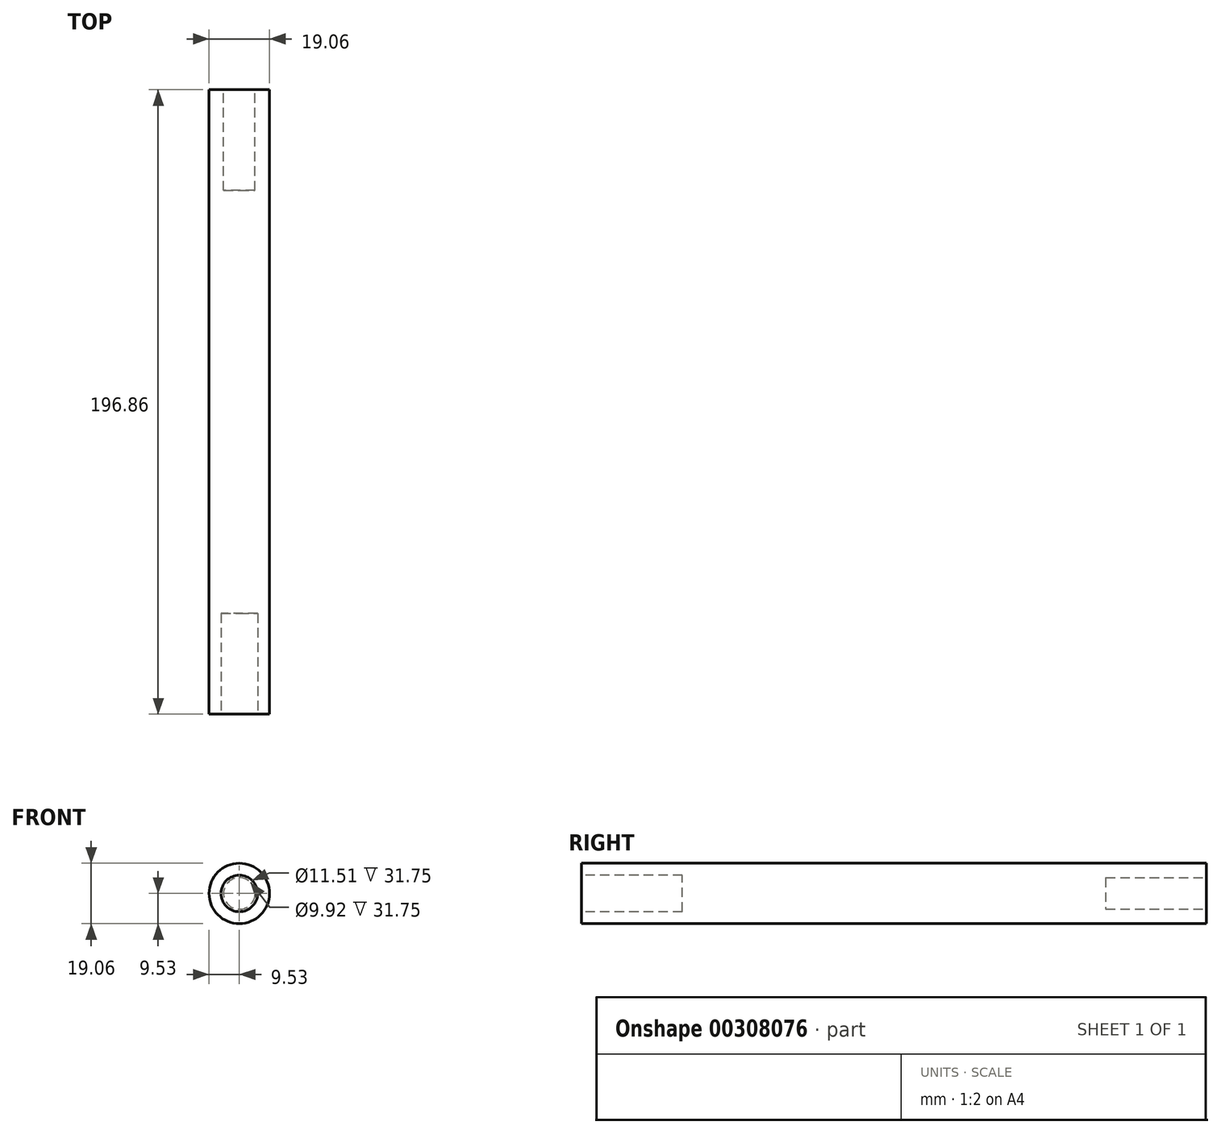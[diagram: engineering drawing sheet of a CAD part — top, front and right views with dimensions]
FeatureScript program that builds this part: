
annotation { "Feature Type Name" : "Feature", "Feature Type Description" : "" }
export const myFeature = defineFeature(function(context is Context, id is Id, definition is map)
    precondition{}
    {
        {
            var Q0;
            Q0=qCreatedBy(makeId("Front.planeOp"),FACE);
            var sketch = newSketch(context, id + "F0", { "sketchPlane" : qUnion([Q0])});
            skCircle(sketch, "E0", {"center": v(0, 0) * mm, "radius": 9.53 * mm});
            skSolve(sketch);
        }
        {
            var Q0;
            Q0=makeQuery(id+"F0.imprint","IMPRINT",FACE,{"disambiguationData":[TD([[makeQuery(id+"F0.imprint","IMPRINT",EDGE,{"derivedFrom":sQuery(id+"F0.wireOp",EDGE,"E0")}),1.0]])]});
            extrude(context, id + "F1", {"entities" : qUnion([Q0]), "endBound" : BoundingType.SYMMETRIC, "depth" : 196.85 * mm, "offsetDistance" : 25.4 * mm});
        }
        {
            var Q0;
            Q0=makeQuery(id+"F1.opExtrude","CAP_FACE",FACE,{"disambiguationData":[OSD([sQuery(id+"F0.wireOp",EDGE,"E0")])],"isStart":false});
            var sketch = newSketch(context, id + "F2", { "sketchPlane" : qUnion([Q0])});
            skCircle(sketch, "E1.0", {"center": v(0, 0) * mm, "radius": 9.53 * mm});
            skCircle(sketch, "E2", {"center": v(0, 0) * mm, "radius": 5.75 * mm});
            skSolve(sketch);
        }
        {
            var Q0;
            Q0=makeQuery(id+"F2.imprint","IMPRINT",FACE,{"disambiguationData":[TD([[makeQuery(id+"F2.imprint","IMPRINT",EDGE,{"derivedFrom":sQuery(id+"F2.wireOp",EDGE,"E2")}),1.0]])]});
            extrude(context, id + "F3", {"entities" : qUnion([Q0]), "operationType" : NewBodyOperationType.REMOVE, "oppositeDirection" : true, "depth" : 31.75 * mm, "offsetDistance" : 25.4 * mm});
        }
        {
            var Q0;
            Q0=makeQuery(id+"F1.opExtrude","CAP_FACE",FACE,{"disambiguationData":[OSD([sQuery(id+"F0.wireOp",EDGE,"E0")])],"isStart":true});
            var sketch = newSketch(context, id + "F4", { "sketchPlane" : qUnion([Q0])});
            skCircle(sketch, "E3.0", {"center": v(0, 0) * mm, "radius": 9.53 * mm});
            skCircle(sketch, "E4", {"center": v(0, 0) * mm, "radius": 4.96 * mm});
            skSolve(sketch);
        }
        {
            var Q0;
            Q0=makeQuery(id+"F4.imprint","IMPRINT",FACE,{"disambiguationData":[TD([[makeQuery(id+"F4.imprint","IMPRINT",EDGE,{"derivedFrom":sQuery(id+"F4.wireOp",EDGE,"E4")}),1.0]])]});
            extrude(context, id + "F5", {"entities" : qUnion([Q0]), "operationType" : NewBodyOperationType.REMOVE, "oppositeDirection" : true, "depth" : 31.75 * mm, "offsetDistance" : 25.4 * mm});
        }
    });
